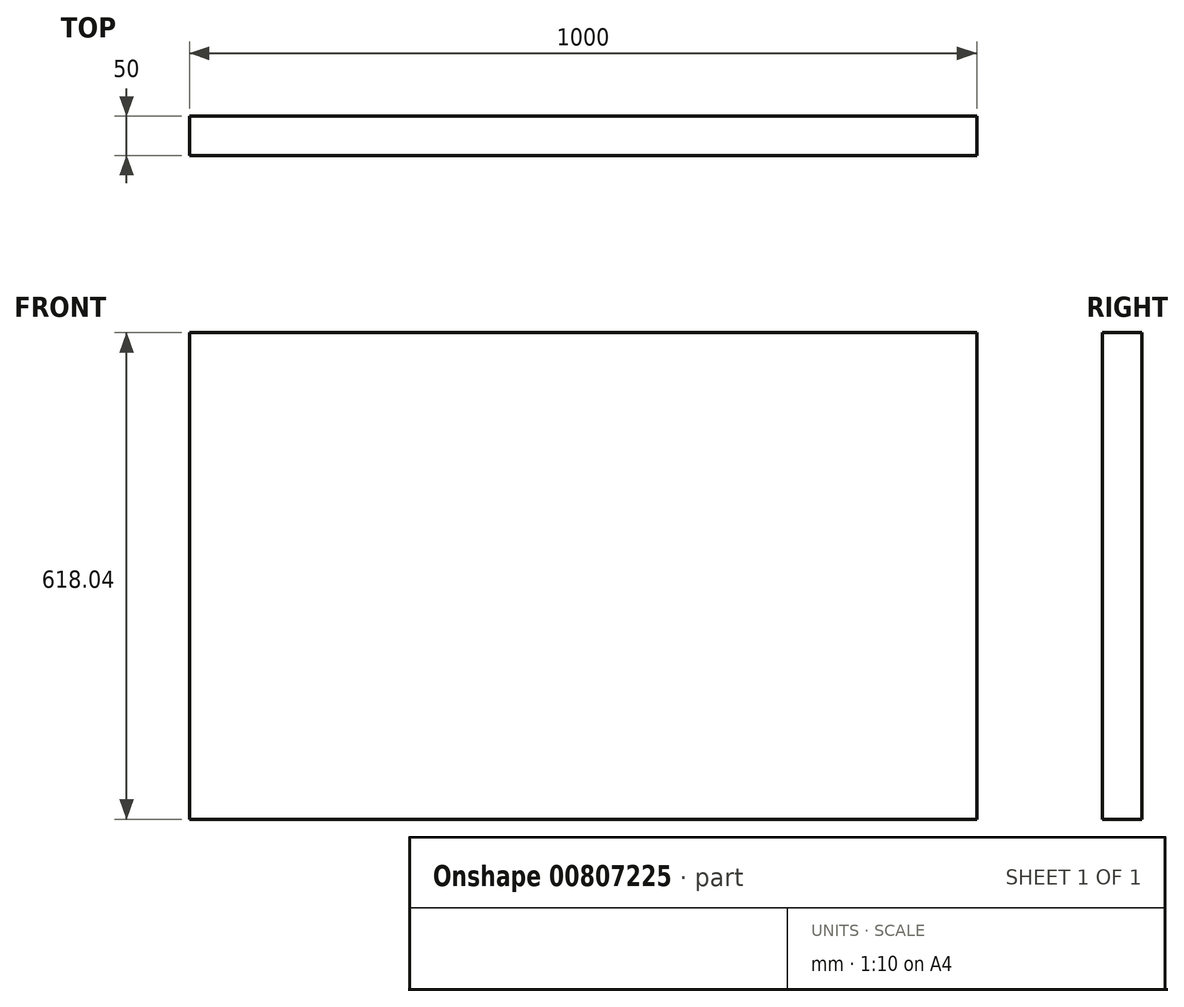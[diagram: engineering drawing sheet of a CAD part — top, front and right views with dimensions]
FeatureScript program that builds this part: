
annotation { "Feature Type Name" : "Feature", "Feature Type Description" : "" }
export const myFeature = defineFeature(function(context is Context, id is Id, definition is map)
    precondition{}
    {
        {
            var Q0;
            Q0=qCreatedBy(makeId("Front.planeOp"),FACE);
            var sketch = newSketch(context, id + "F0", { "sketchPlane" : qUnion([Q0])});
            skLineSegment(sketch, "E0.bottom", {"start": v(-500, 309.03) * mm, "end": v(500, 309.03) * mm});
            skLineSegment(sketch, "E0.top", {"start": v(-500, -309.03) * mm, "end": v(500, -309.03) * mm});
            skLineSegment(sketch, "E0.left", {"start": v(-500, 309.03) * mm, "end": v(-500, -309.03) * mm});
            skLineSegment(sketch, "E0.right", {"start": v(500, 309.03) * mm, "end": v(500, -309.03) * mm});
            skPoint(sketch, "E0.middle", {"position": v(0, 0) * mm});
            skSolve(sketch);
        }
        {
            var Q0;
            Q0=makeQuery(id+"F0.imprint","IMPRINT",FACE,{"disambiguationData":[TD([[makeQuery(id+"F0.imprint","IMPRINT",EDGE,{"derivedFrom":sQuery(id+"F0.wireOp",EDGE,"E0.bottom")}),-1.0]])]});
            extrude(context, id + "F1", {"entities" : qUnion([Q0]), "depth" : 50 * mm, "offsetDistance" : 25 * mm});
        }
    });
